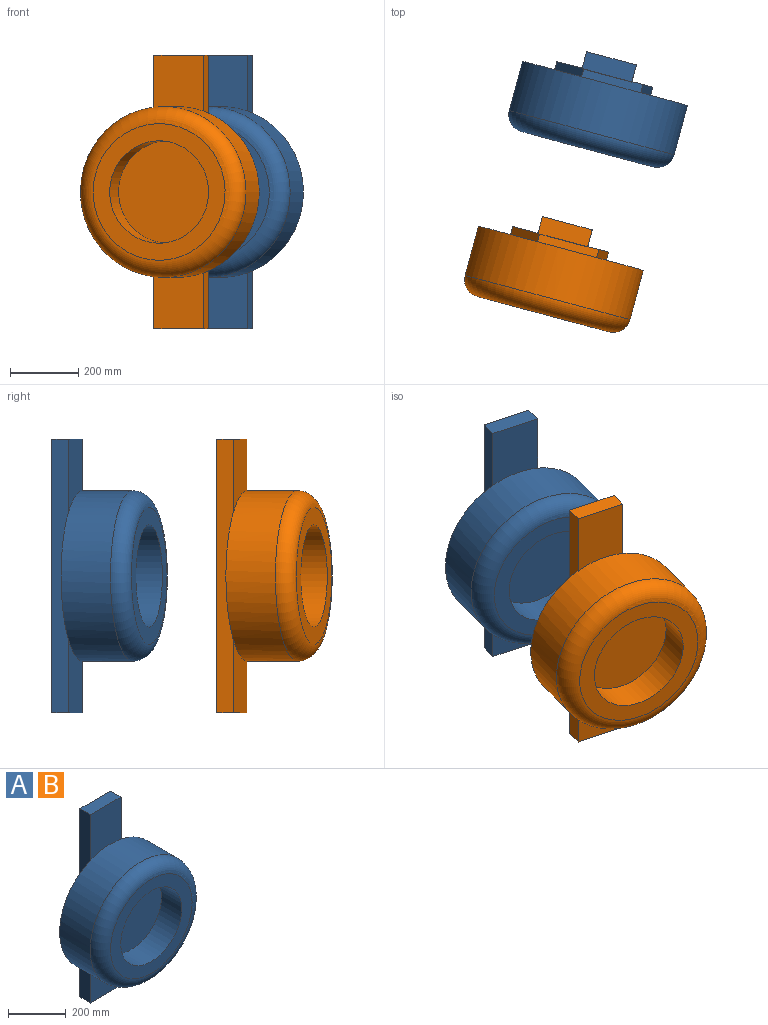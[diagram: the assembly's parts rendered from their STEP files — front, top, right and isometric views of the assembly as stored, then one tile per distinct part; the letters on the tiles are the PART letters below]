
ASSEMBLY  parts=2 mates=1
PART A: 20 faces, bbox 541.2x274.8x800 mm
  f0: plane 179.5x27.8mm, normal (0.15,0,0.99), area 4320.1mm2, adj f2,f5,f9,f10,f13,f17
  f1: plane 161.55x83.02mm, normal (0.46,0,-0.89), area 4374.6mm2, adj f2,f5,f10,f11,f16,f17
  f2: plane 216.81x62.82mm, normal (0,1,0), area 9762.7mm2, adj f0,f1,f10,f17
  f3: cylinder r=250mm len=500mm, axis (0,1,0), area 235619.4mm2, adj f5,f8
  f4: plane 400x400mm, normal (0,-1,0), area 54977.9mm2, adj f6,f8
  f5: plane 500x500mm, normal (0,1,0), area 139588.4mm2, adj f0,f1,f3,f9,f10,f11
  f6: cylinder r=150mm len=300mm, axis (0,1,0), area 94247.8mm2, adj f4,f7
  f7: plane 300x300mm, normal (0,-1,0), area 70685.8mm2, adj f6
  f8: torus R=200mm, axis (0,-1,0), area 114404mm2, adj f3,f4
  f9: plane 162.12x81.9mm, normal (-0.89,0,0.45), area 4523.9mm2, adj f0,f5,f11,f12,f13,f15
  f10: plane 179.3x29.03mm, normal (0.99,0,0.16), area 4540.9mm2, adj f0,f1,f2,f5
  f11: plane 128.88x127.99mm, normal (-0.7,0,-0.71), area 4431mm2, adj f1,f5,f9,f12,f15,f16
  f12: plane 228.26x76.79mm, normal (0,1,0), area 8763.8mm2, adj f9,f11,f15
  f13: plane 285.14x150.83mm, normal (0,-1,0), area 41272.6mm2, adj f0,f9,f15,f17,f18
  f14: plane 800x150.83mm, normal (0,1,0), area 120660.2mm2, adj f15,f17,f18,f19
  f15: plane 800x51.34mm, normal (-1,0,0), area 40734mm2, adj f9,f11,f12,f13,f14,f16,f18,f19
  f16: plane 299.04x150.83mm, normal (0,-1,0), area 41152.9mm2, adj f1,f11,f15,f17,f19
  f17: plane 800x51.34mm, normal (1,0,0), area 40751.1mm2, adj f0,f1,f2,f13,f14,f16,f18,f19
  f18: plane 150.83x51.34mm, normal (0,0,1), area 7744.1mm2, adj f13,f14,f15,f17
  f19: plane 150.83x51.34mm, normal (0,0,-1), area 7744.1mm2, adj f14,f15,f16,f17
PART B: same geometry as A
PLACE A rot(axis=(0,0,-1),15deg) t=(-25.94,488.74,-251.75)mm
PLACE B rot(axis=(0,0,-1),15deg) t=(-155.35,5.77,-251.75)mm fixed
MATE planar A.f3 <-> B.f3  axis (0.26,0.97,0) through (-25.94,488.74,-251.75)mm
